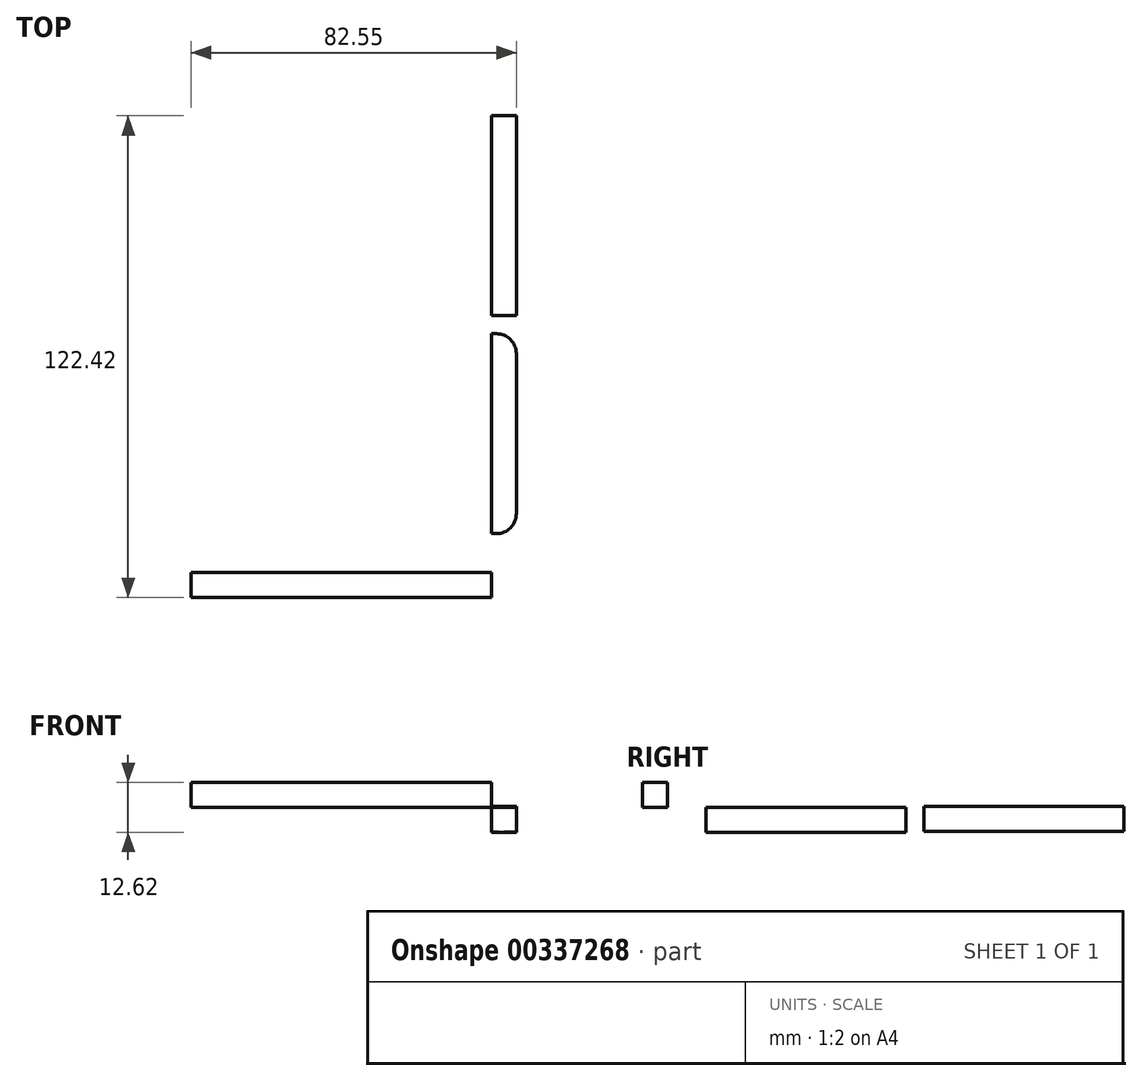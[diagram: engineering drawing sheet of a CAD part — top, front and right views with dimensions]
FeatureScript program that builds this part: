
annotation { "Feature Type Name" : "Feature", "Feature Type Description" : "" }
export const myFeature = defineFeature(function(context is Context, id is Id, definition is map)
    precondition{}
    {
        {
            var Q0;
            Q0=qCreatedBy(makeId("Front.planeOp"),FACE);
            var sketch = newSketch(context, id + "F0", { "sketchPlane" : qUnion([Q0])});
            skLineSegment(sketch, "E0.bottom", {"start": v(-76.2, 34.37) * mm, "end": v(0, 34.37) * mm});
            skLineSegment(sketch, "E0.top", {"start": v(-76.2, 28.02) * mm, "end": v(0, 28.02) * mm});
            skLineSegment(sketch, "E0.left", {"start": v(-76.2, 34.37) * mm, "end": v(-76.2, 28.02) * mm});
            skLineSegment(sketch, "E0.right", {"start": v(0, 34.37) * mm, "end": v(0, 28.02) * mm});
            skSolve(sketch);
        }
        {
            var Q0;
            Q0=makeQuery(id+"F0.imprint","IMPRINT",FACE,{"disambiguationData":[TD([[makeQuery(id+"F0.imprint","IMPRINT",EDGE,{"derivedFrom":sQuery(id+"F0.wireOp",EDGE,"E0.bottom")}),-1.0]])]});
            extrude(context, id + "F1", {"entities" : qUnion([Q0]), "depth" : 6.35 * mm});
        }
        {
            var Q0;
            Q0=qCreatedBy(makeId("Right.planeOp"),FACE);
            var sketch = newSketch(context, id + "F2", { "sketchPlane" : qUnion([Q0])});
            skLineSegment(sketch, "E1.bottom", {"start": v(65.27, 28.32) * mm, "end": v(116.07, 28.32) * mm});
            skLineSegment(sketch, "E1.top", {"start": v(65.27, 21.97) * mm, "end": v(116.07, 21.97) * mm});
            skLineSegment(sketch, "E1.left", {"start": v(65.27, 28.32) * mm, "end": v(65.27, 21.97) * mm});
            skLineSegment(sketch, "E1.right", {"start": v(116.07, 28.32) * mm, "end": v(116.07, 21.97) * mm});
            skSolve(sketch);
        }
        {
            var Q0;
            Q0 = qSketchRegion(id + "F2", true);
            extrude(context, id + "F3", {"entities" : qUnion([Q0]), "depth" : 6.35 * mm});
        }
        {
            var Q0;
            Q0=qCreatedBy(makeId("Right.planeOp"),FACE);
            var sketch = newSketch(context, id + "F4", { "sketchPlane" : qUnion([Q0])});
            skLineSegment(sketch, "E2.bottom", {"start": v(9.88, 28.1) * mm, "end": v(60.68, 28.1) * mm});
            skLineSegment(sketch, "E2.top", {"start": v(9.88, 21.75) * mm, "end": v(60.68, 21.75) * mm});
            skLineSegment(sketch, "E2.left", {"start": v(9.88, 28.1) * mm, "end": v(9.88, 21.75) * mm});
            skLineSegment(sketch, "E2.right", {"start": v(60.68, 28.1) * mm, "end": v(60.68, 21.75) * mm});
            skSolve(sketch);
        }
        {
            var Q0;
            Q0=makeQuery(id+"F4.imprint","IMPRINT",FACE,{"disambiguationData":[TD([[makeQuery(id+"F4.imprint","IMPRINT",EDGE,{"derivedFrom":sQuery(id+"F4.wireOp",EDGE,"E2.bottom")}),-1.0]])]});
            extrude(context, id + "F5", {"entities" : qUnion([Q0]), "depth" : 6.35 * mm});
        }
        {
            var Q0;
            Q0=makeQuery(id+"F5.opExtrude","CAP_EDGE",EDGE,{"disambiguationData":[OSD([sQuery(id+"F4.wireOp",EDGE,"E2.left")])],"isStart":false});
            var Q1;
            Q1=makeQuery(id+"F5.opExtrude","CAP_EDGE",EDGE,{"disambiguationData":[OSD([sQuery(id+"F4.wireOp",EDGE,"E2.right")])],"isStart":false});
            fillet(context, id + "F6", {"entities" : qUnion([Q0, Q1]), "radius" : 5.08 * mm, "tangentPropagation" : true, "allowEdgeOverflow" : false});
        }
    });
